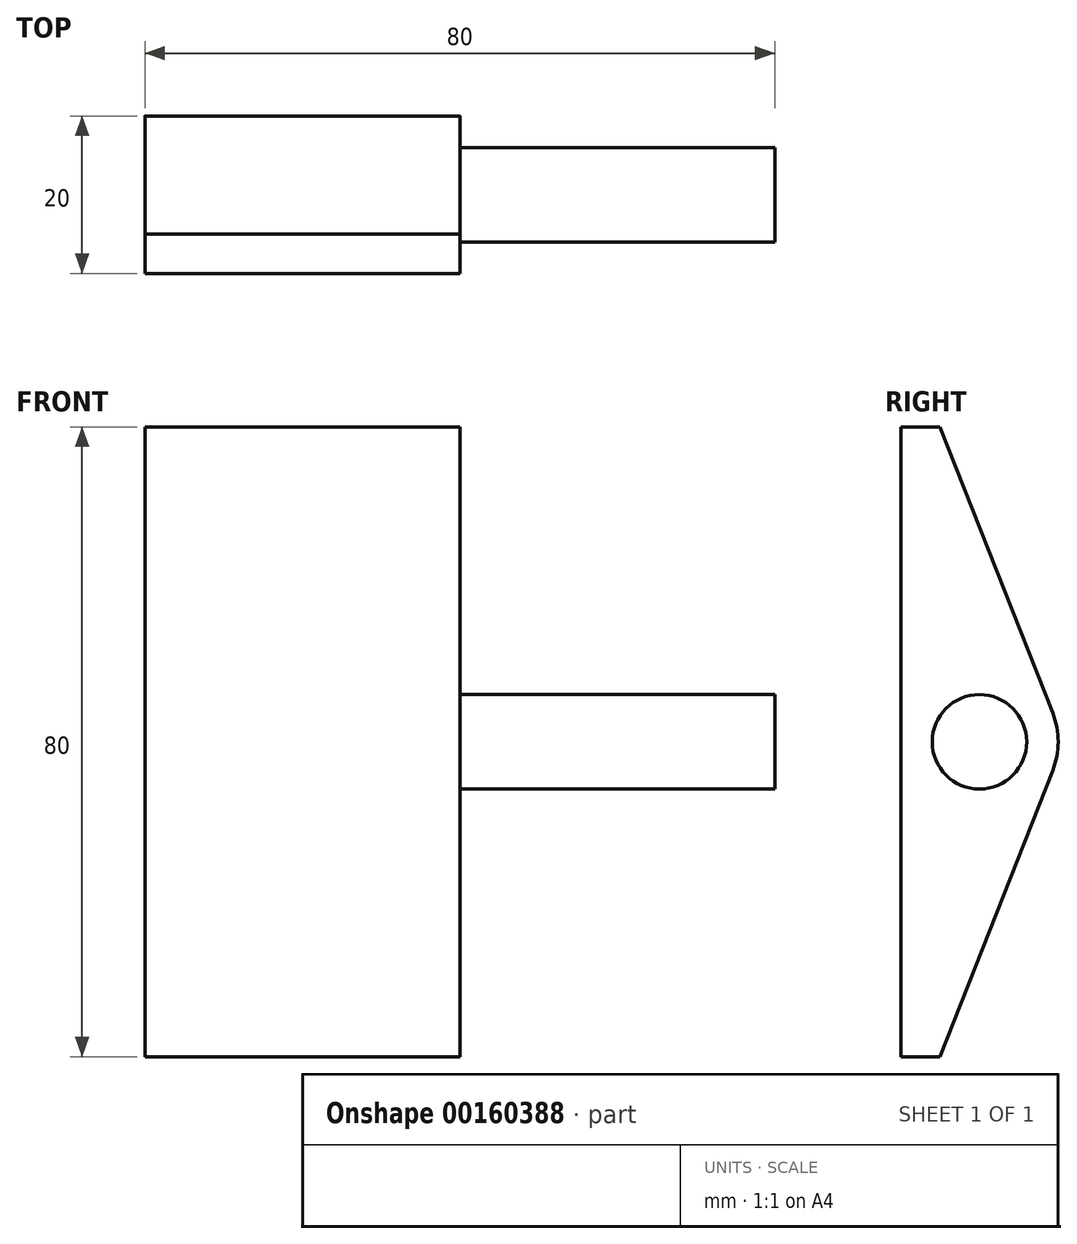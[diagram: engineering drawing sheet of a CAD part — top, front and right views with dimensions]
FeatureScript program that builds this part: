
annotation { "Feature Type Name" : "Feature", "Feature Type Description" : "" }
export const myFeature = defineFeature(function(context is Context, id is Id, definition is map)
    precondition{}
    {
        {
            var Q0;
            Q0=qCreatedBy(makeId("Right.planeOp"),FACE);
            var sketch = newSketch(context, id + "F0", { "sketchPlane" : qUnion([Q0])});
            skCircle(sketch, "E0", {"center": v(0, 0) * mm, "radius": 10 * mm});
            skLineSegment(sketch, "E1", {"start": v(-10, 40) * mm, "end": v(-10, 0) * mm});
            skLineSegment(sketch, "E2", {"start": v(-10, 40) * mm, "end": v(-5, 40) * mm});
            skLineSegment(sketch, "E3", {"start": v(9.3, 3.66) * mm, "end": v(-5, 40) * mm});
            skSolve(sketch);
        }
        {
            var Q0;
            Q0 = qSketchRegion(id + "F0", true);
            extrude(context, id + "F1", {"entities" : qUnion([Q0]), "depth" : 40 * mm});
        }
        {
            var Q0;
            Q0=makeQuery(id+"F1.opExtrude","CAP_FACE",FACE,{"disambiguationData":[OSD([sQuery(id+"F0.wireOp",EDGE,"E0"),sQuery(id+"F0.wireOp",EDGE,"E1"),sQuery(id+"F0.wireOp",EDGE,"E2"),sQuery(id+"F0.wireOp",EDGE,"E3")])],"isStart":false});
            var sketch = newSketch(context, id + "F2", { "sketchPlane" : qUnion([Q0])});
            skCircle(sketch, "E4", {"center": v(0, 0) * mm, "radius": 6 * mm});
            skSolve(sketch);
        }
        {
            var Q0;
            Q0=makeQuery(id+"F2.imprint","IMPRINT",FACE,{"disambiguationData":[TD([[makeQuery(id+"F2.imprint","IMPRINT",EDGE,{"derivedFrom":sQuery(id+"F2.wireOp",EDGE,"E4")}),1.0]])]});
            extrude(context, id + "F3", {"entities" : qUnion([Q0]), "operationType" : NewBodyOperationType.REMOVE, "endBound" : BoundingType.THROUGH_ALL, "oppositeDirection" : true, "depth" : 25 * mm});
        }
        {
            var Q0;
            Q0=qCreatedBy(makeId("Right.planeOp"),FACE);
            var sketch = newSketch(context, id + "F4", { "sketchPlane" : qUnion([Q0])});
            skCircle(sketch, "E5", {"center": v(0, 0) * mm, "radius": 10 * mm});
            skLineSegment(sketch, "E6", {"start": v(-10, 0) * mm, "end": v(-10, -40) * mm});
            skLineSegment(sketch, "E7", {"start": v(-10, -40) * mm, "end": v(-5, -40) * mm});
            skLineSegment(sketch, "E8", {"start": v(-5, -40) * mm, "end": v(9.3, -3.66) * mm});
            skSolve(sketch);
        }
        {
            var Q0;
            Q0 = qSketchRegion(id + "F4", true);
            extrude(context, id + "F5", {"entities" : qUnion([Q0]), "depth" : 40 * mm});
        }
        {
            var Q0;
            Q0=makeQuery(id+"F5.opExtrude","CAP_FACE",FACE,{"disambiguationData":[OSD([sQuery(id+"F4.wireOp",EDGE,"E5"),sQuery(id+"F4.wireOp",EDGE,"E6"),sQuery(id+"F4.wireOp",EDGE,"E7"),sQuery(id+"F4.wireOp",EDGE,"E8")])],"isStart":false});
            var sketch = newSketch(context, id + "F6", { "sketchPlane" : qUnion([Q0])});
            skCircle(sketch, "E9", {"center": v(0, 0) * mm, "radius": 6 * mm});
            skSolve(sketch);
        }
        {
            var Q0;
            Q0 = qSketchRegion(id + "F6", true);
            extrude(context, id + "F7", {"entities" : qUnion([Q0]), "operationType" : NewBodyOperationType.ADD, "depth" : 40 * mm});
        }
    });
